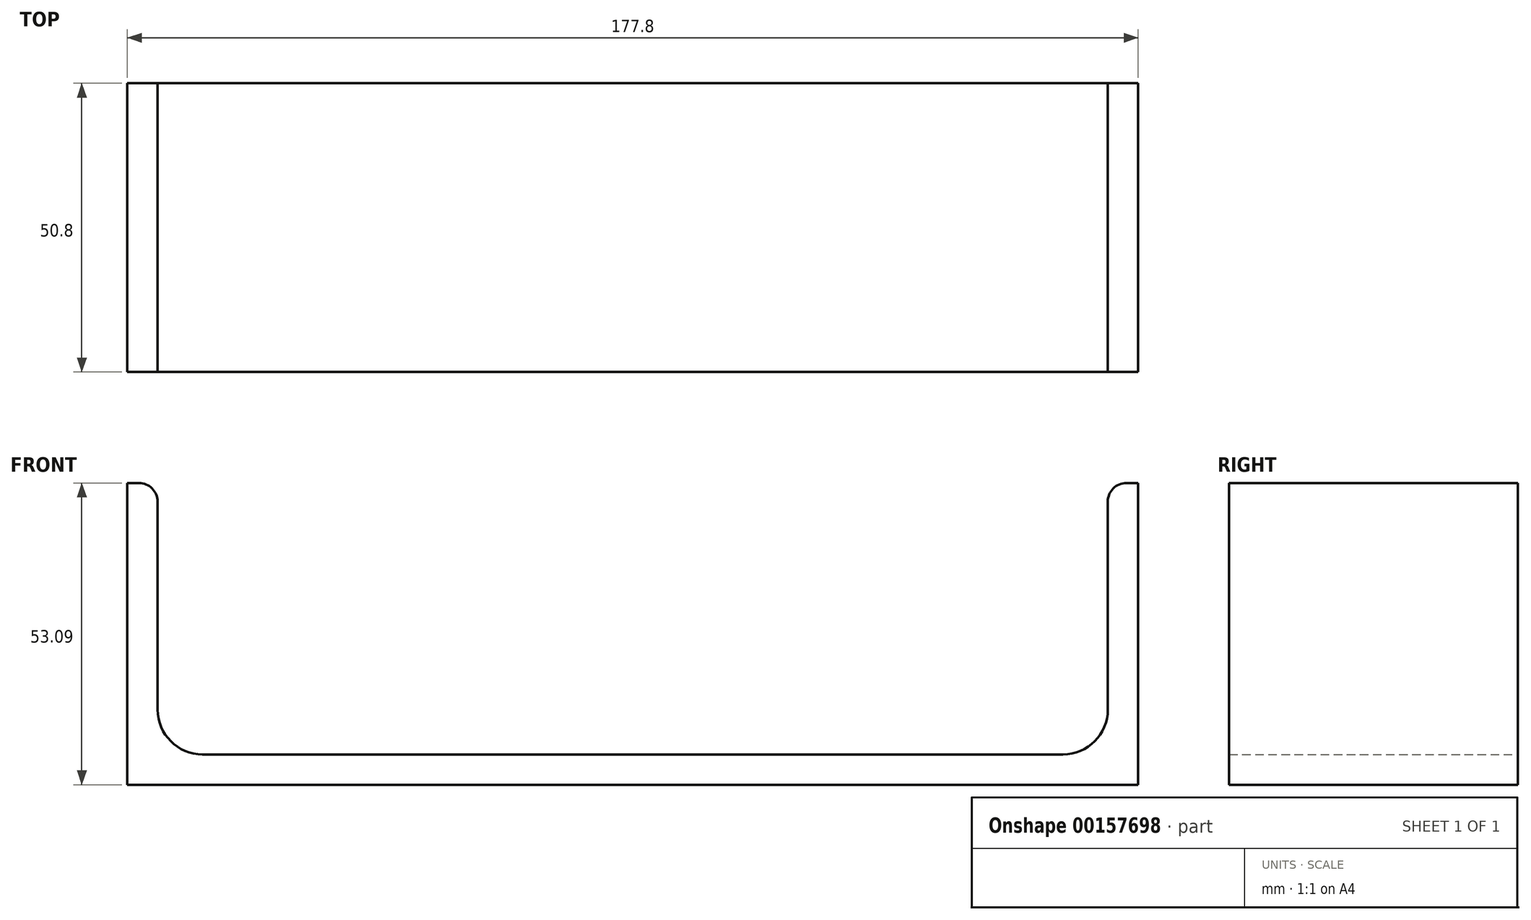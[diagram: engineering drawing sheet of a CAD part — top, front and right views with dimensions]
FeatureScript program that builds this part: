
annotation { "Feature Type Name" : "Feature", "Feature Type Description" : "" }
export const myFeature = defineFeature(function(context is Context, id is Id, definition is map)
    precondition{}
    {
        {
            var Q0;
            Q0=qCreatedBy(makeId("Front.planeOp"),FACE);
            var sketch = newSketch(context, id + "F0", { "sketchPlane" : qUnion([Q0])});
            skLineSegment(sketch, "E0", {"start": v(0, 0) * mm, "end": v(-88.9, 0) * mm});
            skLineSegment(sketch, "E1", {"start": v(0, 0) * mm, "end": v(88.9, 0) * mm});
            skLineSegment(sketch, "E2", {"start": v(-88.9, 0) * mm, "end": v(-88.9, 53.09) * mm});
            skLineSegment(sketch, "E3", {"start": v(88.9, 0) * mm, "end": v(88.9, 53.09) * mm});
            skPoint(sketch, "E4.visualSharp", {"position": v(83.57, 5.33) * mm});
            skLineSegment(sketch, "E5", {"start": v(-88.9, 53.09) * mm, "end": v(-86.87, 53.09) * mm});
            skLineSegment(sketch, "E6", {"start": v(-83.57, 49.78) * mm, "end": v(-83.57, 13.2) * mm});
            skLineSegment(sketch, "E7", {"start": v(88.9, 53.09) * mm, "end": v(86.87, 53.09) * mm});
            skLineSegment(sketch, "E8", {"start": v(83.57, 49.78) * mm, "end": v(83.57, 13.2) * mm});
            skLineSegment(sketch, "E9", {"start": v(75.7, 5.33) * mm, "end": v(-75.7, 5.33) * mm});
            skArc(sketch, "E10.filletArc", {"start": v(75.7, 5.33) * mm, "mid": v(81.26, 7.64) * mm, "end": v(83.57, 13.2) * mm});
            skPoint(sketch, "E11.visualSharp", {"position": v(-83.57, 5.33) * mm});
            skArc(sketch, "E11.filletArc", {"start": v(-83.57, 13.2) * mm, "mid": v(-81.26, 7.64) * mm, "end": v(-75.7, 5.33) * mm});
            skPoint(sketch, "E12.visualSharp", {"position": v(-83.57, 53.09) * mm});
            skArc(sketch, "E12.filletArc", {"start": v(-83.57, 49.78) * mm, "mid": v(-84.53, 52.12) * mm, "end": v(-86.87, 53.09) * mm});
            skPoint(sketch, "E13.visualSharp", {"position": v(83.57, 53.09) * mm});
            skArc(sketch, "E13.filletArc", {"start": v(86.87, 53.09) * mm, "mid": v(84.53, 52.12) * mm, "end": v(83.57, 49.78) * mm});
            skSolve(sketch);
        }
        {
            var Q0;
            Q0 = qSketchRegion(id + "F0", true);
            extrude(context, id + "F1", {"entities" : qUnion([Q0]), "endBound" : BoundingType.SYMMETRIC, "depth" : 50.8 * mm});
        }
    });
